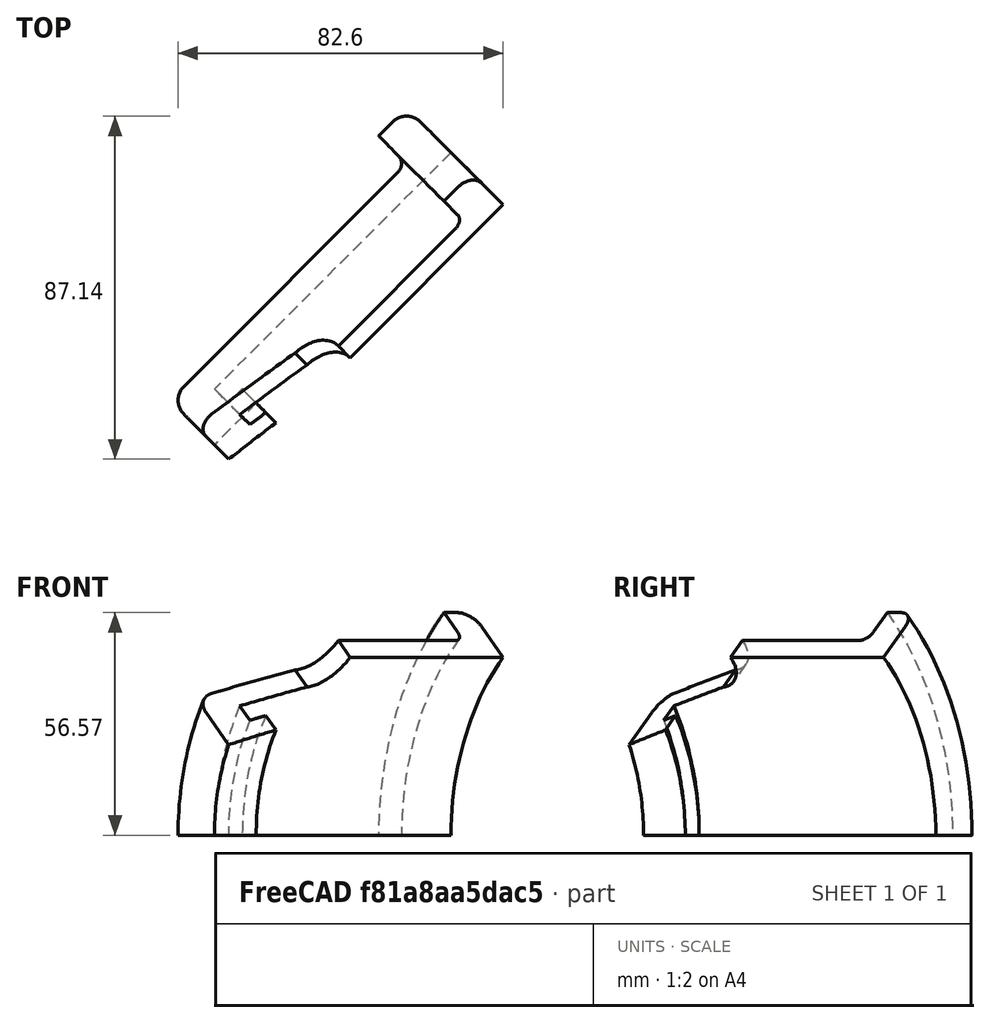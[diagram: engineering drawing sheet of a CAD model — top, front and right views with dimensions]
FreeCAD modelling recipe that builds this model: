
FCSTD DOCUMENT  (FreeCAD 0.15R4671 (Git))
Label: sphere_support_cyls4_w2
License: All rights reserved
LicenseURL: http://en.wikipedia.org/wiki/All_rights_reserved
objects: Part::Cut×11, Part::Box×8, Part::Cylinder×6, Part::Fillet×3, Part::MultiFuse×2
note: 30 computed .brp shape members not serialized (recipe doc carries the construction recipe); baked Part::Feature solids carry a one-line shape summary decoded from their .brp

FEATURE [Part::Cylinder] Cylinder  label="Base_Cylinder"
  Angle = 360
  Height = 10
  Radius = 80
FEATURE [Part::Cylinder] Cylinder001  label="Body_Cylinder"
  Angle = 360
  Height = 90
  Placement = pos=(0,0,5) rot=(0,0,1;0rad)
  Radius = 70
FEATURE [Part::MultiFuse] Fusion  label="Core_Fusion"
  Shapes = -> [Cylinder,Cylinder001]
FEATURE [Part::Cylinder] Cylinder002  label="Inner_Hole"
  Angle = 360
  Height = 85
  Radius = 64
FEATURE [Part::Cut] Cut
  Base = -> Fusion
  Tool = -> Cylinder002
FEATURE [Part::Cylinder] Cylinder003  label="Inner_Lip"
  Angle = 360
  Height = 10
  Placement = pos=(0,0,80) rot=(0,0,1;0rad)
  Radius = 59
FEATURE [Part::MultiFuse] Fusion001
  Shapes = -> [Cut,Cylinder003]
FEATURE [Part::Cylinder] Cylinder004  label="Through_Hole"
  Angle = 360
  Height = 100
  Radius = 54
FEATURE [Part::Cut] Cut001
  Base = -> Fusion001
  Tool = -> Cylinder004
FEATURE [Part::Fillet] Fillet
  Base = -> Cut001
  Edges = 1 edges r=3: [Edge12]
FEATURE [Part::Fillet] Fillet001
  Base = -> Fillet
  Edges = 1 edges r=5: [Edge11]
FEATURE [Part::Fillet] Fillet002
  Base = -> Fillet001
  Edges = 1 edges r=5: [Edge13]
FEATURE [Part::Cylinder] Cylinder005  label="Bearing_Holes"
  Angle = 360
  Height = 180
  Placement = pos=(0,90,65) rot=(1,0,0;1.5708rad)
  Radius = 10
FEATURE [Part::Cut] Cut002
  Base = -> Fillet002
  Tool = -> Cylinder005
FEATURE [Part::Box] Box  label="Bearing_Slot"
  Height = 35
  Length = 20
  Placement = pos=(-10,48,65) rot=(0,0,1;0rad)
  Width = 25
FEATURE [Part::Cut] Cut003
  Base = -> Cut002
  Tool = -> Box
FEATURE [Part::Box] Box001  label="Cube"
  Height = 35
  Length = 10
  Placement = pos=(0,48,65) rot=(0,1,0;0.261799rad)
  Width = 25
FEATURE [Part::Cut] Cut004
  Base = -> Cut003
  Tool = -> Box001
FEATURE [Part::Box] Box002  label="Cube001"
  Height = 35
  Length = 10
  Placement = pos=(-9.95,48,64) rot=(0,-1,0;0.261799rad)
  Width = 25
FEATURE [Part::Cut] Cut005
  Base = -> Cut004
  Tool = -> Box002
FEATURE [Part::Box] Box003  label="Tab_Cut_R"
  Height = 80
  Length = 20
  Placement = pos=(63,-10,20) rot=(0,0,1;0rad)
  Width = 20
FEATURE [Part::Cut] Cut006
  Base = -> Cut005
  Tool = -> Box003
FEATURE [Part::Box] Box004  label="Tab_Cut_L"
  Height = 80
  Length = 20
  Placement = pos=(-83,-10,20) rot=(0,0,1;0rad)
  Width = 20
FEATURE [Part::Cut] Cut007
  Base = -> Cut006
  Tool = -> Box004
FEATURE [Part::Box] Box005  label="Cube002"
  Height = 100
  Length = 100
  Width = 100
FEATURE [Part::Cut] Cut008
  Base = -> Cut007
  Tool = -> Box005
FEATURE [Part::Box] Box006  label="Cube003"
  Height = 100
  Length = 200
  Placement = pos=(71,-71,0) rot=(0,0,1;2.35619rad)
  Width = 100
FEATURE [Part::Cut] Cut009
  Base = -> Cut008
  Placement = pos=(0,0,0) rot=(0.707107,-0.707107,0;1.5708rad)
  Tool = -> Box006
FEATURE [Part::Box] Box007  label="Cube004"
  Height = 100
  Length = 100
  Placement = pos=(0,0,0) rot=(0,0,-1;2.35619rad)
  Width = 100
FEATURE [Part::Cut] Cut010
  Base = -> Cut009
  Tool = -> Box007
